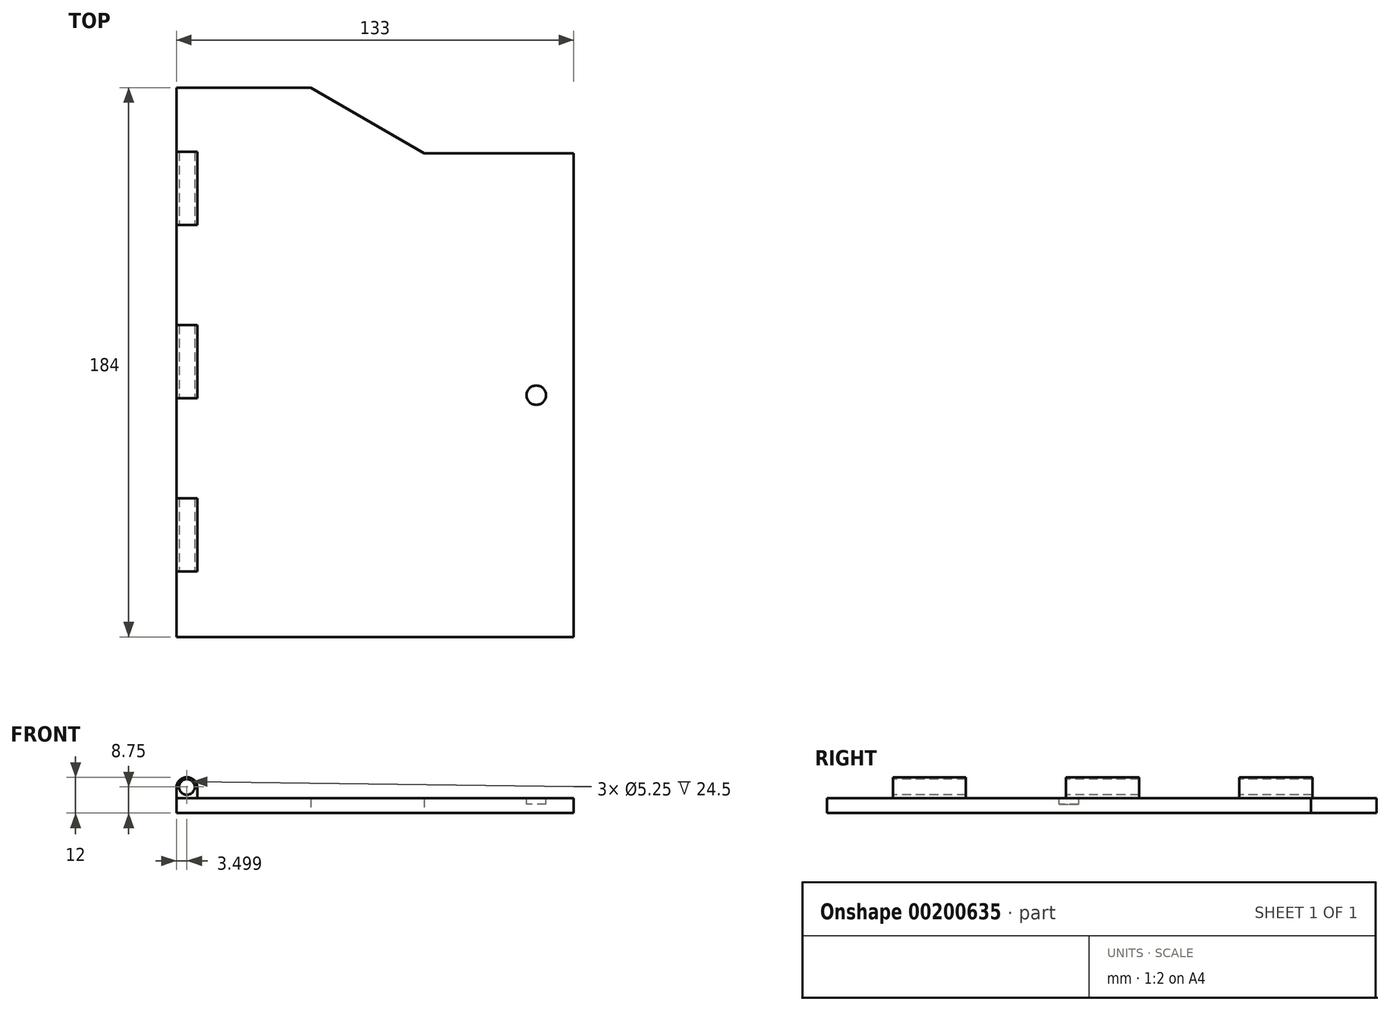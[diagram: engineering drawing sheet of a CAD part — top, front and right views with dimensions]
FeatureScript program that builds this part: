
annotation { "Feature Type Name" : "Feature", "Feature Type Description" : "" }
export const myFeature = defineFeature(function(context is Context, id is Id, definition is map)
    precondition{}
    {
        {
            var Q0;
            Q0=qCreatedBy(makeId("Top.planeOp"),FACE);
            var sketch = newSketch(context, id + "F0", { "sketchPlane" : qUnion([Q0])});
            skLineSegment(sketch, "E0", {"start": v(-79, 142.7) * mm, "end": v(-34, 142.7) * mm});
            skLineSegment(sketch, "E1", {"start": v(-34, 142.7) * mm, "end": v(4, 120.7) * mm});
            skLineSegment(sketch, "E2", {"start": v(4, 120.7) * mm, "end": v(54, 120.7) * mm});
            skLineSegment(sketch, "E3.top", {"start": v(-79, -41.3) * mm, "end": v(54, -41.3) * mm});
            skLineSegment(sketch, "E4", {"start": v(54, 120.7) * mm, "end": v(54, -41.3) * mm});
            skLineSegment(sketch, "E5.bottom", {"start": v(-79, 121.2) * mm, "end": v(-72, 121.2) * mm});
            skLineSegment(sketch, "E5.top", {"start": v(-79, 96.7) * mm, "end": v(-72, 96.7) * mm});
            skLineSegment(sketch, "E5.right", {"start": v(-72, 121.2) * mm, "end": v(-72, 96.7) * mm});
            skLineSegment(sketch, "E6.bottom", {"start": v(-79, 5.2) * mm, "end": v(-72, 5.2) * mm});
            skLineSegment(sketch, "E6.top", {"start": v(-79, -19.3) * mm, "end": v(-72, -19.3) * mm});
            skLineSegment(sketch, "E6.right", {"start": v(-72, 5.2) * mm, "end": v(-72, -19.3) * mm});
            skLineSegment(sketch, "E7.bottom", {"start": v(-79, 63.2) * mm, "end": v(-72, 63.2) * mm});
            skLineSegment(sketch, "E7.top", {"start": v(-79, 38.7) * mm, "end": v(-72, 38.7) * mm});
            skLineSegment(sketch, "E7.right", {"start": v(-72, 63.2) * mm, "end": v(-72, 38.7) * mm});
            skLineSegment(sketch, "E8", {"start": v(-79, 142.7) * mm, "end": v(-79, 121.2) * mm});
            skLineSegment(sketch, "E9", {"start": v(-79, 96.7) * mm, "end": v(-79, 121.2) * mm});
            skLineSegment(sketch, "E10", {"start": v(-79, 96.7) * mm, "end": v(-79, 63.2) * mm});
            skLineSegment(sketch, "E11", {"start": v(-79, 63.2) * mm, "end": v(-79, 38.7) * mm});
            skLineSegment(sketch, "E12", {"start": v(-79, 38.7) * mm, "end": v(-79, 5.2) * mm});
            skLineSegment(sketch, "E13", {"start": v(-79, 5.2) * mm, "end": v(-79, -19.3) * mm});
            skLineSegment(sketch, "E14", {"start": v(-79, -19.3) * mm, "end": v(-79, -41.3) * mm});
            skSolve(sketch);
        }
        {
            var Q0;
            Q0=makeQuery(id+"F0.imprint","IMPRINT",FACE,{"disambiguationData":[TD([[makeQuery(id+"F0.imprint","IMPRINT",EDGE,{"derivedFrom":sQuery(id+"F0.wireOp",EDGE,"E0")}),-1.0]])]});
            var Q1;
            Q1=makeQuery(id+"F0.imprint","IMPRINT",FACE,{"disambiguationData":[TD([[makeQuery(id+"F0.imprint","IMPRINT",EDGE,{"derivedFrom":sQuery(id+"F0.wireOp",EDGE,"E5.bottom")}),-1.0]])]});
            var Q2;
            Q2=makeQuery(id+"F0.imprint","IMPRINT",FACE,{"disambiguationData":[TD([[makeQuery(id+"F0.imprint","IMPRINT",EDGE,{"derivedFrom":sQuery(id+"F0.wireOp",EDGE,"E7.bottom")}),-1.0]])]});
            var Q3;
            Q3=makeQuery(id+"F0.imprint","IMPRINT",FACE,{"disambiguationData":[TD([[makeQuery(id+"F0.imprint","IMPRINT",EDGE,{"derivedFrom":sQuery(id+"F0.wireOp",EDGE,"E6.bottom")}),-1.0]])]});
            extrude(context, id + "F1", {"entities" : qUnion([Q0, Q1, Q2, Q3]), "depth" : 5 * mm});
        }
        {
            var Q0;
            Q0=makeQuery(id+"F1.opExtrude","CAP_FACE",FACE,{"disambiguationData":[OSD([sQuery(id+"F0.wireOp",EDGE,"E0"),sQuery(id+"F0.wireOp",EDGE,"E1"),sQuery(id+"F0.wireOp",EDGE,"E2"),sQuery(id+"F0.wireOp",EDGE,"E3.top"),sQuery(id+"F0.wireOp",EDGE,"E4"),sQuery(id+"F0.wireOp",EDGE,"E8"),sQuery(id+"F0.wireOp",EDGE,"E9"),sQuery(id+"F0.wireOp",EDGE,"E10"),sQuery(id+"F0.wireOp",EDGE,"E11"),sQuery(id+"F0.wireOp",EDGE,"E12"),sQuery(id+"F0.wireOp",EDGE,"E13"),sQuery(id+"F0.wireOp",EDGE,"E14")])],"isStart":false});
            var sketch = newSketch(context, id + "F2", { "sketchPlane" : qUnion([Q0])});
            skLineSegment(sketch, "E15", {"start": v(-79, 142.7) * mm, "end": v(-34, 142.7) * mm});
            skLineSegment(sketch, "E16", {"start": v(-34, 142.7) * mm, "end": v(4, 120.7) * mm});
            skLineSegment(sketch, "E17", {"start": v(4, 120.7) * mm, "end": v(54, 120.7) * mm});
            skLineSegment(sketch, "E18.top", {"start": v(-79, -41.3) * mm, "end": v(54, -41.3) * mm});
            skLineSegment(sketch, "E19", {"start": v(54, 120.7) * mm, "end": v(54, -41.3) * mm});
            skLineSegment(sketch, "E20.bottom", {"start": v(-79, 121.2) * mm, "end": v(-72, 121.2) * mm});
            skLineSegment(sketch, "E20.top", {"start": v(-79, 96.7) * mm, "end": v(-72, 96.7) * mm});
            skLineSegment(sketch, "E20.right", {"start": v(-72, 121.2) * mm, "end": v(-72, 96.7) * mm});
            skLineSegment(sketch, "E21.bottom", {"start": v(-79, 5.2) * mm, "end": v(-72, 5.2) * mm});
            skLineSegment(sketch, "E21.top", {"start": v(-79, -19.3) * mm, "end": v(-72, -19.3) * mm});
            skLineSegment(sketch, "E21.right", {"start": v(-72, 5.2) * mm, "end": v(-72, -19.3) * mm});
            skLineSegment(sketch, "E22.bottom", {"start": v(-79, 63.2) * mm, "end": v(-72, 63.2) * mm});
            skLineSegment(sketch, "E22.top", {"start": v(-79, 38.7) * mm, "end": v(-72, 38.7) * mm});
            skLineSegment(sketch, "E22.right", {"start": v(-72, 63.2) * mm, "end": v(-72, 38.7) * mm});
            skLineSegment(sketch, "E23", {"start": v(-79, 142.7) * mm, "end": v(-79, 121.2) * mm});
            skLineSegment(sketch, "E24", {"start": v(-79, 96.7) * mm, "end": v(-79, 121.2) * mm});
            skLineSegment(sketch, "E25", {"start": v(-79, 96.7) * mm, "end": v(-79, 63.2) * mm});
            skLineSegment(sketch, "E26", {"start": v(-79, 63.2) * mm, "end": v(-79, 38.7) * mm});
            skLineSegment(sketch, "E27", {"start": v(-79, 38.7) * mm, "end": v(-79, 5.2) * mm});
            skLineSegment(sketch, "E28", {"start": v(-79, 5.2) * mm, "end": v(-79, -19.3) * mm});
            skLineSegment(sketch, "E29", {"start": v(-79, -19.3) * mm, "end": v(-79, -41.3) * mm});
            skSolve(sketch);
        }
        {
            var Q0;
            Q0=makeQuery(id+"F2.imprint","IMPRINT",FACE,{"disambiguationData":[TD([[makeQuery(id+"F2.imprint","IMPRINT",EDGE,{"derivedFrom":sQuery(id+"F2.wireOp",EDGE,"E20.bottom")}),-1.0]])]});
            var Q1;
            Q1=makeQuery(id+"F2.imprint","IMPRINT",FACE,{"disambiguationData":[TD([[makeQuery(id+"F2.imprint","IMPRINT",EDGE,{"derivedFrom":sQuery(id+"F2.wireOp",EDGE,"E22.bottom")}),-1.0]])]});
            var Q2;
            Q2=makeQuery(id+"F2.imprint","IMPRINT",FACE,{"disambiguationData":[TD([[makeQuery(id+"F2.imprint","IMPRINT",EDGE,{"derivedFrom":sQuery(id+"F2.wireOp",EDGE,"E21.bottom")}),-1.0]])]});
            extrude(context, id + "F3", {"entities" : qUnion([Q0, Q1, Q2]), "operationType" : NewBodyOperationType.ADD, "depth" : 7 * mm});
        }
        {
            var Q0;
            Q0=makeQuery(id+"F3.opExtrude","CAP_EDGE",EDGE,{"disambiguationData":[OSD([sQuery(id+"F2.wireOp",EDGE,"E20.right")])],"isStart":false});
            var Q1;
            Q1=makeQuery(id+"F3.opExtrude","CAP_EDGE",EDGE,{"disambiguationData":[OSD([sQuery(id+"F2.wireOp",EDGE,"E22.right")])],"isStart":false});
            var Q2;
            Q2=makeQuery(id+"F3.opExtrude","CAP_EDGE",EDGE,{"disambiguationData":[OSD([sQuery(id+"F2.wireOp",EDGE,"E26")])],"isStart":false});
            var Q3;
            Q3=makeQuery(id+"F3.opExtrude","CAP_EDGE",EDGE,{"disambiguationData":[OSD([sQuery(id+"F2.wireOp",EDGE,"E24")])],"isStart":false});
            var Q4;
            Q4=makeQuery(id+"F3.opExtrude","CAP_EDGE",EDGE,{"disambiguationData":[OSD([sQuery(id+"F2.wireOp",EDGE,"E21.right")])],"isStart":false});
            var Q5;
            Q5=makeQuery(id+"F3.opExtrude","CAP_EDGE",EDGE,{"disambiguationData":[OSD([sQuery(id+"F2.wireOp",EDGE,"E28")])],"isStart":false});
            fillet(context, id + "F4", {"entities" : qUnion([Q0, Q1, Q2, Q3, Q4, Q5]), "radius" : 3.5 * mm, "tangentPropagation" : true, "allowEdgeOverflow" : false});
        }
        {
            var Q0;
            Q0=makeQuery(id+"F3.opExtrude","SWEPT_FACE",FACE,{"disambiguationData":[OSD([sQuery(id+"F2.wireOp",EDGE,"E21.top")])]});
            var sketch = newSketch(context, id + "F5", { "sketchPlane" : qUnion([Q0])});
            skCircle(sketch, "E30", {"center": v(-75.5, 8.75) * mm, "radius": 2.63 * mm});
            skSolve(sketch);
        }
        {
            var Q0;
            Q0 = qSketchRegion(id + "F5", true);
            extrude(context, id + "F6", {"entities" : qUnion([Q0]), "operationType" : NewBodyOperationType.REMOVE, "endBound" : BoundingType.THROUGH_ALL, "oppositeDirection" : true, "depth" : 25 * mm});
        }
        {
            var Q0;
            Q0=makeQuery(id+"F1.opExtrude","CAP_FACE",FACE,{"disambiguationData":[OSD([sQuery(id+"F0.wireOp",EDGE,"E0"),sQuery(id+"F0.wireOp",EDGE,"E1"),sQuery(id+"F0.wireOp",EDGE,"E2"),sQuery(id+"F0.wireOp",EDGE,"E3.top"),sQuery(id+"F0.wireOp",EDGE,"E4"),sQuery(id+"F0.wireOp",EDGE,"E8"),sQuery(id+"F0.wireOp",EDGE,"E9"),sQuery(id+"F0.wireOp",EDGE,"E10"),sQuery(id+"F0.wireOp",EDGE,"E11"),sQuery(id+"F0.wireOp",EDGE,"E12"),sQuery(id+"F0.wireOp",EDGE,"E13"),sQuery(id+"F0.wireOp",EDGE,"E14")])],"isStart":false});
            var sketch = newSketch(context, id + "F7", { "sketchPlane" : qUnion([Q0])});
            skLineSegment(sketch, "E31", {"start": v(41.5, 120.7) * mm, "end": v(41.5, 42.96) * mm, "construction": true});
            skCircle(sketch, "E32", {"center": v(41.5, 39.7) * mm, "radius": 3.25 * mm});
            skLineSegment(sketch, "E33.trimOffspring", {"start": v(41.5, 36.46) * mm, "end": v(41.5, -41.3) * mm, "construction": true});
            skSolve(sketch);
        }
        {
            var Q0;
            Q0=makeQuery(id+"F7.imprint","IMPRINT",FACE,{"disambiguationData":[TD([[makeQuery(id+"F7.imprint","IMPRINT",EDGE,{"derivedFrom":sQuery(id+"F7.wireOp",EDGE,"E32")}),1.0]])]});
            extrude(context, id + "F8", {"entities" : qUnion([Q0]), "operationType" : NewBodyOperationType.REMOVE, "oppositeDirection" : true, "depth" : 2 * mm});
        }
    });
